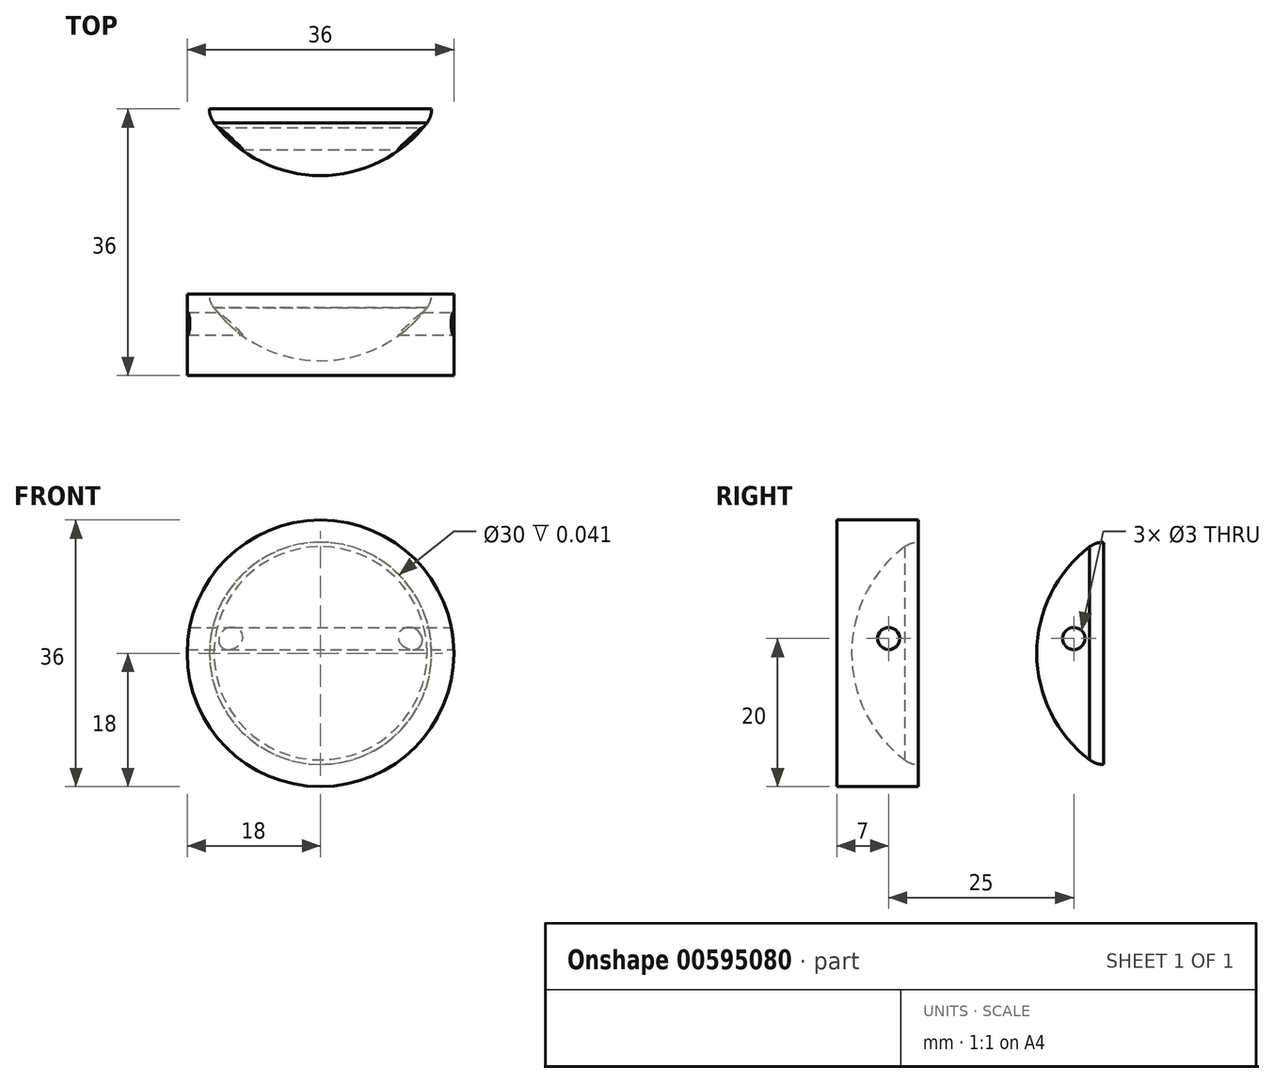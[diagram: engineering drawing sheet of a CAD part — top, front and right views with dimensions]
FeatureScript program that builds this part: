
annotation { "Feature Type Name" : "Feature", "Feature Type Description" : "" }
export const myFeature = defineFeature(function(context is Context, id is Id, definition is map)
    precondition{}
    {
        {
            var Q0;
            Q0=qCreatedBy(makeId("Right.planeOp"),FACE);
            var sketch = newSketch(context, id + "F0", { "sketchPlane" : qUnion([Q0])});
            skLineSegment(sketch, "E0", {"start": v(0, 15) * mm, "end": v(0, -15) * mm});
            skCircle(sketch, "E1", {"center": v(10.06, 0) * mm, "radius": 18.06 * mm});
            skCircle(sketch, "E2", {"center": v(-3, 2) * mm, "radius": 1.5 * mm});
            skLineSegment(sketch, "E3", {"start": v(-8, 0) * mm, "end": v(-8, -11.86) * mm});
            skLineSegment(sketch, "E4", {"start": v(10.06, 18.06) * mm, "end": v(10.06, -18.06) * mm});
            skSolve(sketch);
        }
        {
            var Q0;
            {var subQ0=sQuery(id+"F0.wireOp",EDGE,"E0");Q0=makeQuery(id+"F0.imprint","IMPRINT",FACE,{"disambiguationData":[TD([[makeQuery(id+"F0.imprint","IMPRINT",EDGE,{"derivedFrom":subQ0}),1.0]])]});}
            var Q1;
            {var subQ0=sQuery(id+"F0.wireOp",EDGE,"E0");Q1=makeQuery(id+"F0.imprint","IMPRINT",FACE,{"disambiguationData":[TD([[makeQuery(id+"F0.imprint","IMPRINT",EDGE,{"derivedFrom":subQ0}),-1.0]])]});}
            var Q2;
            Q2=makeQuery(id+"F0.imprint","IMPRINT",FACE,{"disambiguationData":[TD([[makeQuery(id+"F0.imprint","IMPRINT",EDGE,{"derivedFrom":sQuery(id+"F0.wireOp",EDGE,"E2")}),1.0]])]});
            var Q3;
            Q3=sQuery(id+"F0.wireOp",EDGE,"E4");
            revolve(context, id + "F1", {"surfaceOperationType" : NewSurfaceOperationType.NEW, "entities" : qUnion([Q0, Q1, Q2]), "axis" : qUnion([Q3]), "revolveType" : RevolveType.FULL});
        }
        {
            var Q0;
            {var subQ0=sQuery(id+"F0.wireOp",EDGE,"E4");Q0=makeQuery(id+"F0.imprint","IMPRINT",FACE,{"disambiguationData":[TD([[makeQuery(id+"F0.imprint","IMPRINT",EDGE,{"derivedFrom":subQ0}),1.0]])]});}
            var Q1;
            {var subQ0=sQuery(id+"F0.wireOp",EDGE,"E0");Q1=makeQuery(id+"F0.imprint","IMPRINT",FACE,{"disambiguationData":[TD([[makeQuery(id+"F0.imprint","IMPRINT",EDGE,{"derivedFrom":subQ0}),1.0]])]});}
            var Q2;
            Q2=makeQuery(id+"F0.imprint","IMPRINT",FACE,{"disambiguationData":[TD([[makeQuery(id+"F0.imprint","IMPRINT",EDGE,{"derivedFrom":sQuery(id+"F0.wireOp",EDGE,"E2")}),1.0]])]});
            extrude(context, id + "F2", {"entities" : qUnion([Q0, Q1, Q2]), "operationType" : NewBodyOperationType.REMOVE, "oppositeDirection" : true, "depth" : 25 * mm, "offsetDistance" : 25 * mm, "hasSecondDirection" : true, "secondDirectionOppositeDirection" : false, "secondDirectionDepth" : 25 * mm});
        }
        {
            var Q0;
            Q0=makeQuery(id+"F2.boolean.opBoolean","COPY",FACE,{"derivedFrom":makeQuery(id+"F2.opExtrude","SWEPT_FACE",FACE,{"disambiguationData":[OSD([sQuery(id+"F0.wireOp",EDGE,"E0")])]})});
            extrude(context, id + "F3", {"entities" : qUnion([Q0]), "operationType" : NewBodyOperationType.ADD, "depth" : 1 * mm, "offsetDistance" : 25 * mm});
        }
        {
            var Q0;
            {var subQ0=sQuery(id+"F0.wireOp",EDGE,"E1");var subQ1=sQuery(id+"F0.wireOp",EDGE,"E0");Q0=makeQuery(id+"F3.boolean.opBoolean","MERGE",EDGE,{"derivedFrom":[makeQuery(id+"F2.boolean.opBoolean","INTERSECT",EDGE,{"derivedFrom":[makeQuery(id+"F1.opRevolve","SWEPT_FACE",FACE,{"disambiguationData":[OSD([subQ0])]}),makeQuery(id+"F2.opExtrude","SWEPT_FACE",FACE,{"disambiguationData":[OSD([subQ1])]})]}),makeQuery(id+"F3.opExtrude","CAP_EDGE",EDGE,{"disambiguationData":[OSD([subQ1,subQ0])],"isStart":true})]});}
            fillet(context, id + "F4", {"entities" : qUnion([Q0]), "radius" : 3 * mm, "tangentPropagation" : true, "allowEdgeOverflow" : false});
        }
        {
            var Q0;
            Q0=makeQuery(id+"F3.opExtrude","CAP_FACE",FACE,{"disambiguationData":[OSD([sQuery(id+"F0.wireOp",EDGE,"E0")])],"isStart":false});
            var sketch = newSketch(context, id + "F5", { "sketchPlane" : qUnion([Q0])});
            skCircle(sketch, "E5", {"center": v(0, 0) * mm, "radius": 18 * mm});
            skSolve(sketch);
        }
        {
            var Q0;
            Q0=makeQuery(id+"F5.imprint","IMPRINT",FACE,{"disambiguationData":[TD([[makeQuery(id+"F5.imprint","IMPRINT",EDGE,{"derivedFrom":sQuery(id+"F5.wireOp",EDGE,"E5")}),1.0]])]});
            var Q1;
            Q1=makeQuery(id+"F5.imprint","IMPRINT",FACE,{"disambiguationData":[TD([[makeQuery(id+"F5.imprint","IMPRINT",EDGE,{"derivedFrom":makeQuery(id+"F3.opExtrude","CAP_EDGE",EDGE,{"disambiguationData":[OSD([sQuery(id+"F0.wireOp",EDGE,"E0"),sQuery(id+"F0.wireOp",EDGE,"E1")])],"isStart":false})}),1.0]])]});
            extrude(context, id + "F6", {"entities" : qUnion([Q0, Q1]), "oppositeDirection" : true, "depth" : 11 * mm, "offsetDistance" : 25 * mm});
        }
        {
            var Q0;
            Q0=makeQuery(id+"F0.imprint","IMPRINT",FACE,{"disambiguationData":[TD([[makeQuery(id+"F0.imprint","IMPRINT",EDGE,{"derivedFrom":sQuery(id+"F0.wireOp",EDGE,"E2")}),1.0]])]});
            extrude(context, id + "F7", {"entities" : qUnion([Q0]), "operationType" : NewBodyOperationType.REMOVE, "oppositeDirection" : true, "depth" : 25 * mm, "offsetDistance" : 25 * mm, "hasSecondDirection" : true, "secondDirectionOppositeDirection" : false, "secondDirectionDepth" : 25 * mm});
        }
        {
            var Q0;
            Q0=makeQuery(id+"F1.opRevolve","SWEPT_BODY",BODY,{"disambiguationData":[OSD([sQuery(id+"F0.wireOp",EDGE,"E1"),sQuery(id+"F0.wireOp",EDGE,"E4")])]});
            var Q1;
            Q1=makeQuery(id+"F6.opExtrude","SWEPT_BODY",BODY,{"disambiguationData":[OSD([sQuery(id+"F5.wireOp",EDGE,"E5")])]});
            booleanBodies(context, id + "F8", {"operationType" : BooleanOperationType.SUBTRACTION, "tools" : qUnion([Q0]), "targets" : qUnion([Q1]), "keepTools" : true});
        }
        {
            var Q0;
            Q0=makeQuery(id+"F6.opExtrude","SWEPT_BODY",BODY,{"disambiguationData":[OSD([sQuery(id+"F5.wireOp",EDGE,"E5")])]});
            var Q1;
            Q1=makeQuery(id+"F3.opExtrude","CAP_FACE",FACE,{"disambiguationData":[OSD([sQuery(id+"F0.wireOp",EDGE,"E0")])],"isStart":false});
            transform(context, id + "F9", {"entities" : qUnion([Q0]), "transformType" : TransformType.TRANSLATION_DISTANCE, "transformDirection" : qUnion([Q1]), "distance" : 25 * mm, "oppositeDirection" : true, "makeCopy" : false});
        }
    });
